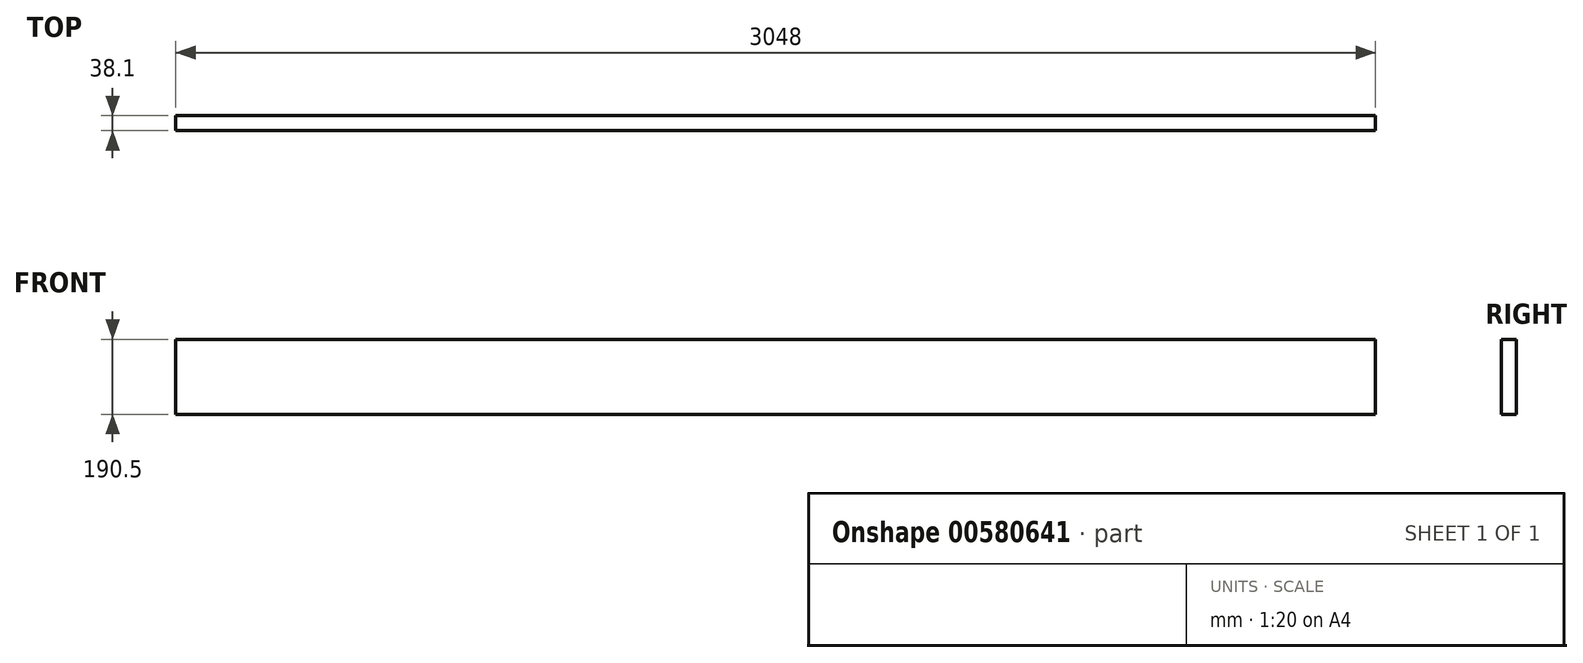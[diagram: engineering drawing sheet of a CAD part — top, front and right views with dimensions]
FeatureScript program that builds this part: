
annotation { "Feature Type Name" : "Feature", "Feature Type Description" : "" }
export const myFeature = defineFeature(function(context is Context, id is Id, definition is map)
    precondition{}
    {
        {
            var Q0;
            Q0=qCreatedBy(makeId("Top.planeOp"),FACE);
            var sketch = newSketch(context, id + "F0", { "sketchPlane" : qUnion([Q0])});
            skLineSegment(sketch, "E0.bottom", {"start": v(1524, -19.05) * mm, "end": v(-1524, -19.05) * mm});
            skLineSegment(sketch, "E0.top", {"start": v(1524, 19.05) * mm, "end": v(-1524, 19.05) * mm});
            skLineSegment(sketch, "E0.left", {"start": v(1524, -19.05) * mm, "end": v(1524, 19.05) * mm});
            skLineSegment(sketch, "E0.right", {"start": v(-1524, -19.05) * mm, "end": v(-1524, 19.05) * mm});
            skPoint(sketch, "E0.middle", {"position": v(0, 0) * mm});
            skSolve(sketch);
        }
        {
            var Q0;
            Q0=makeQuery(id+"F0.imprint","IMPRINT",FACE,{"disambiguationData":[TD([[makeQuery(id+"F0.imprint","IMPRINT",EDGE,{"derivedFrom":sQuery(id+"F0.wireOp",EDGE,"E0.bottom")}),-1.0]])]});
            extrude(context, id + "F1", {"entities" : qUnion([Q0]), "depth" : 190.5 * mm, "offsetDistance" : 25.4 * mm});
        }
    });
